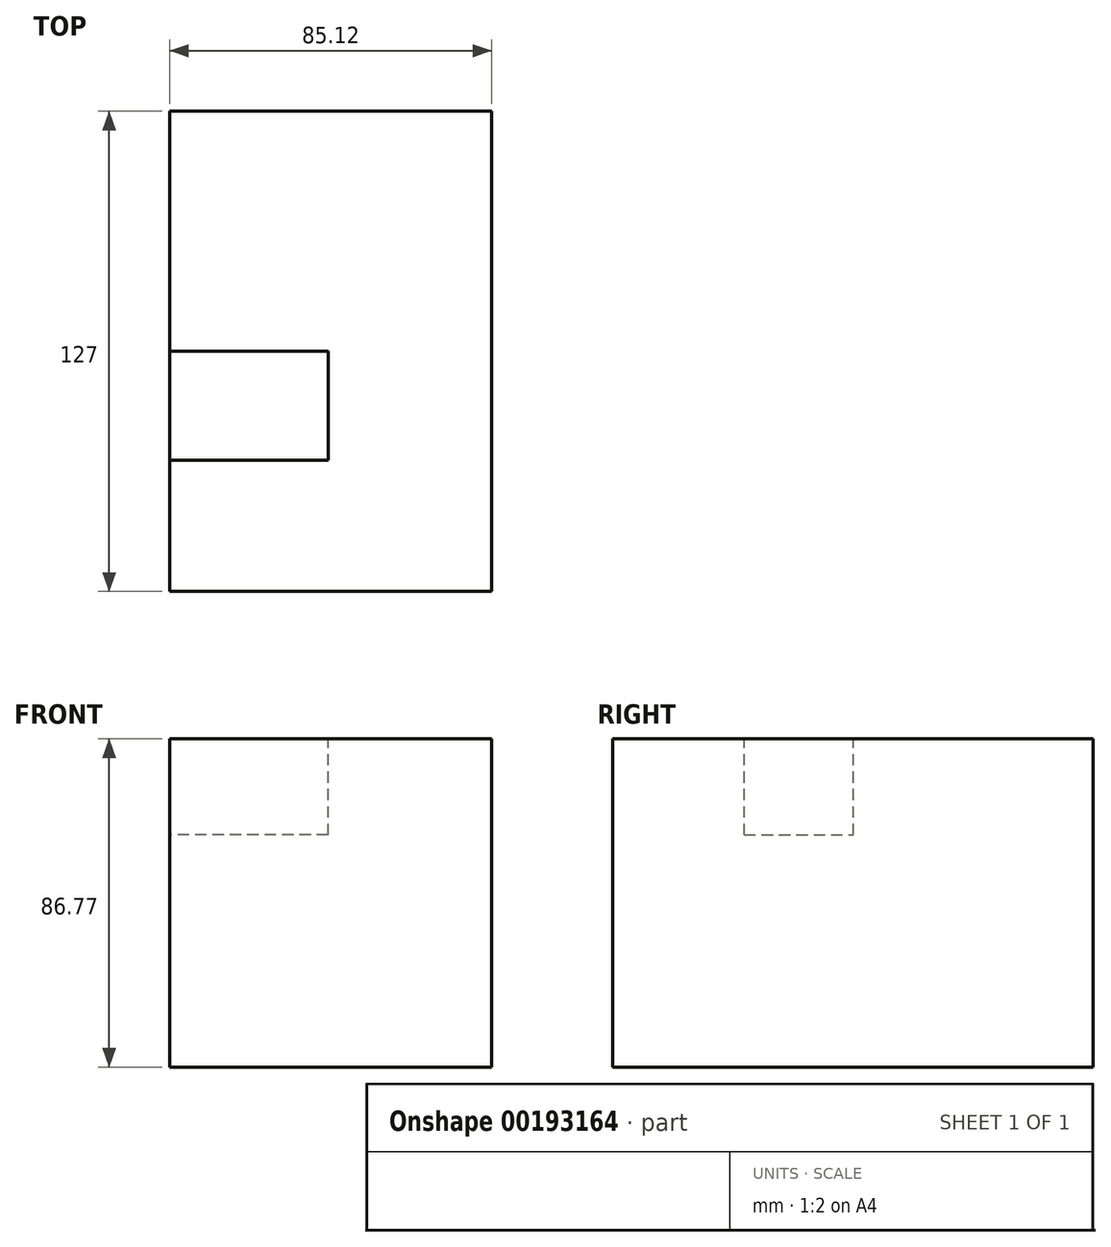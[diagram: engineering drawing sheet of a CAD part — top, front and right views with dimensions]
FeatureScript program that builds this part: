
annotation { "Feature Type Name" : "Feature", "Feature Type Description" : "" }
export const myFeature = defineFeature(function(context is Context, id is Id, definition is map)
    precondition{}
    {
        {
            var Q0;
            Q0=qCreatedBy(makeId("Front.planeOp"),FACE);
            var sketch = newSketch(context, id + "F5", { "sketchPlane" : qUnion([Q0])});
            skLineSegment(sketch, "E0.bottom", {"start": v(0, 0) * mm, "end": v(85.12, 0) * mm});
            skLineSegment(sketch, "E0.top", {"start": v(0, 86.77) * mm, "end": v(85.12, 86.77) * mm});
            skLineSegment(sketch, "E0.left", {"start": v(0, 0) * mm, "end": v(0, 86.77) * mm});
            skLineSegment(sketch, "E0.right", {"start": v(85.12, 0) * mm, "end": v(85.12, 86.77) * mm});
            skSolve(sketch);
        }
        {
            var Q0;
            Q0=makeQuery(id+"F5.imprint","IMPRINT",FACE,{"disambiguationData":[TD([[makeQuery(id+"F5.imprint","IMPRINT",EDGE,{"derivedFrom":sQuery(id+"F5.wireOp",EDGE,"E0.bottom")}),1.0]])]});
            var sketch = newSketch(context, id + "F0", { "sketchPlane" : qUnion([Q0])});
            skSolve(sketch);
        }
        {
            var Q0;
            Q0=makeQuery(id+"F0.imprint","IMPRINT",FACE,{"disambiguationData":[TD([[makeQuery(id+"F0.imprint","IMPRINT",EDGE,{"derivedFrom":makeQuery(id+"F5.imprint","IMPRINT",EDGE,{"derivedFrom":sQuery(id+"F5.wireOp",EDGE,"E0.bottom")})}),1.0]])]});
            extrude(context, id + "F6", {"entities" : qUnion([Q0]), "depth" : 127 * mm});
        }
        {
            var Q0;
            Q0=makeQuery(id+"F6.opExtrude","SWEPT_FACE",FACE,{"disambiguationData":[OSD([sQuery(id+"F5.wireOp",EDGE,"E0.top")])]});
            var sketch = newSketch(context, id + "F7", { "sketchPlane" : qUnion([Q0])});
            skLineSegment(sketch, "E1.bottom", {"start": v(41.89, -63.43) * mm, "end": v(0, -63.43) * mm});
            skLineSegment(sketch, "E1.top", {"start": v(41.89, -92.29) * mm, "end": v(0, -92.29) * mm});
            skLineSegment(sketch, "E1.left", {"start": v(41.89, -63.43) * mm, "end": v(41.89, -92.29) * mm});
            skLineSegment(sketch, "E1.right", {"start": v(0, -63.43) * mm, "end": v(0, -92.29) * mm});
            skSolve(sketch);
        }
        {
            var Q0;
            Q0=makeQuery(id+"F7.imprint","IMPRINT",FACE,{"disambiguationData":[TD([[makeQuery(id+"F7.imprint","IMPRINT",EDGE,{"derivedFrom":sQuery(id+"F7.wireOp",EDGE,"E1.bottom")}),1.0]])]});
            extrude(context, id + "F1", {"entities" : qUnion([Q0]), "operationType" : NewBodyOperationType.REMOVE, "oppositeDirection" : true, "depth" : 25.4 * mm});
        }
    });
